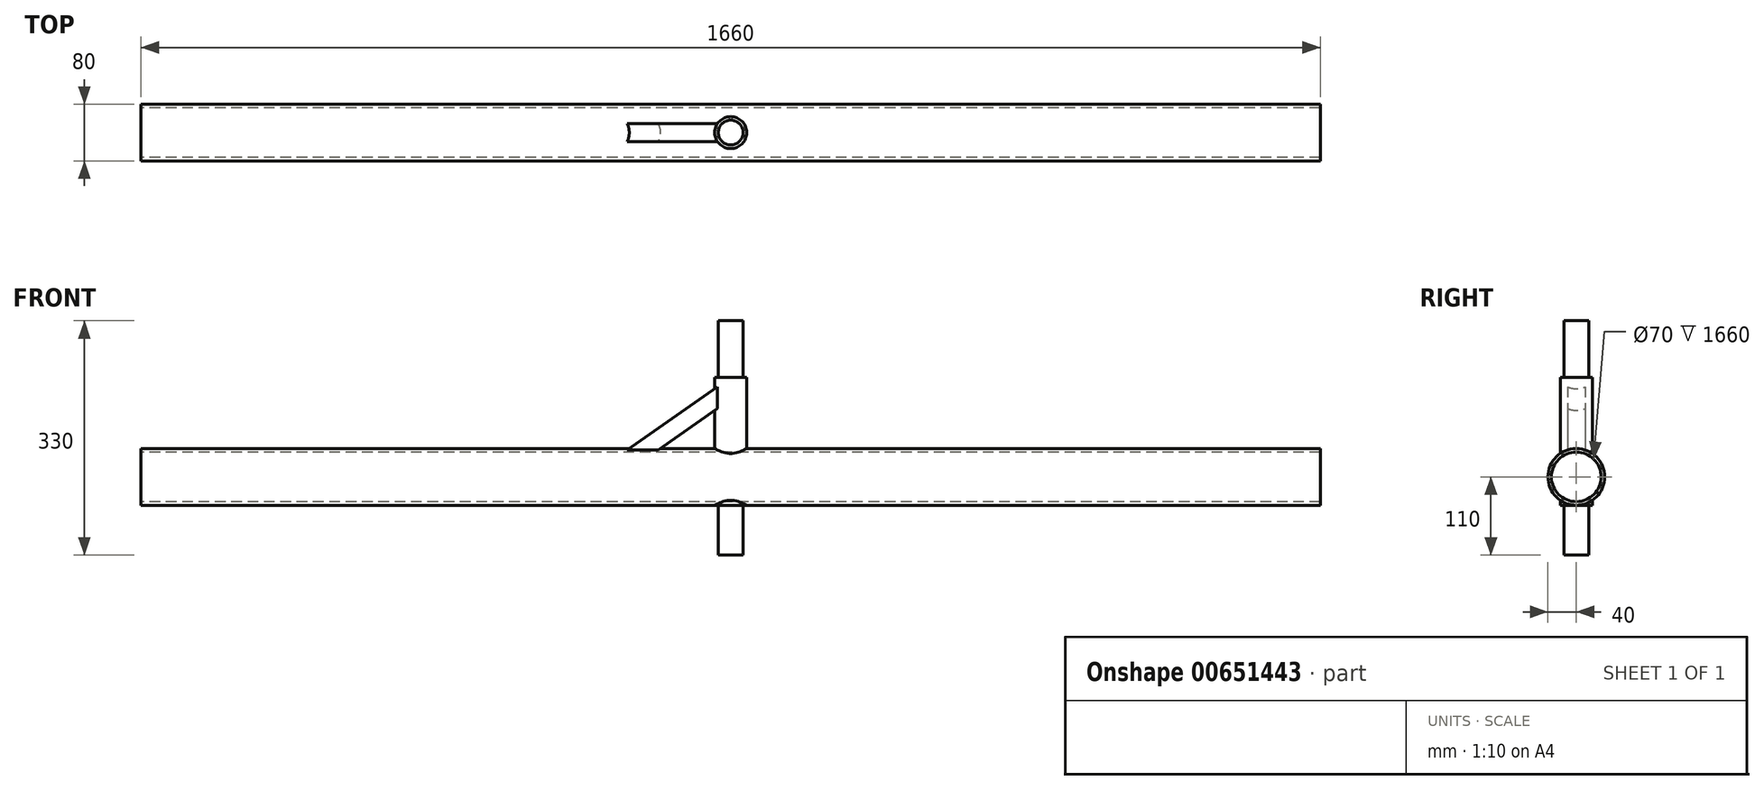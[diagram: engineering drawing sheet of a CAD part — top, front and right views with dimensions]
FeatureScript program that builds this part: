
annotation { "Feature Type Name" : "Feature", "Feature Type Description" : "" }
export const myFeature = defineFeature(function(context is Context, id is Id, definition is map)
    precondition{}
    {
        {
            var Q0;
            Q0=qCreatedBy(makeId("Right.planeOp"),FACE);
            var sketch = newSketch(context, id + "F0", { "sketchPlane" : qUnion([Q0])});
            skCircle(sketch, "E0", {"center": v(0, 0) * mm, "radius": 40 * mm});
            skSolve(sketch);
        }
        {
            var Q0;
            Q0=makeQuery(id+"F0.imprint","IMPRINT",FACE,{"disambiguationData":[TD([[makeQuery(id+"F0.imprint","IMPRINT",EDGE,{"derivedFrom":sQuery(id+"F0.wireOp",EDGE,"E0")}),1.0]])]});
            extrude(context, id + "F1", {"entities" : qUnion([Q0]), "depth" : 830 * mm, "offsetDistance" : 25 * mm, "hasSecondDirection" : true, "secondDirectionOppositeDirection" : true, "secondDirectionDepth" : 830 * mm});
        }
        {
            var Q0;
            Q0=qCreatedBy(makeId("Top.planeOp"),FACE);
            var sketch = newSketch(context, id + "F2", { "sketchPlane" : qUnion([Q0])});
            skCircle(sketch, "E1", {"center": v(0, 0) * mm, "radius": 22.5 * mm});
            skSolve(sketch);
        }
        {
            var Q0;
            Q0 = qSketchRegion(id + "F2", true);
            extrude(context, id + "F3", {"entities" : qUnion([Q0]), "operationType" : NewBodyOperationType.ADD, "depth" : 140 * mm, "offsetDistance" : 25 * mm, "hasSecondDirection" : true, "secondDirectionOppositeDirection" : true, "secondDirectionDepth" : 40 * mm});
        }
        {
            var Q0;
            Q0=makeQuery(id+"F3.opExtrude","CAP_FACE",FACE,{"disambiguationData":[OSD([sQuery(id+"F2.wireOp",EDGE,"E1")])],"isStart":false});
            var sketch = newSketch(context, id + "F4", { "sketchPlane" : qUnion([Q0])});
            skCircle(sketch, "E2", {"center": v(0, 0) * mm, "radius": 17.5 * mm});
            skSolve(sketch);
        }
        {
            var Q0;
            Q0 = qSketchRegion(id + "F4", true);
            var Q1;
            Q1=makeQuery(id+"F3.opExtrude","CAP_FACE",FACE,{"disambiguationData":[OSD([sQuery(id+"F2.wireOp",EDGE,"E1")])],"isStart":true});
            extrude(context, id + "F5", {"entities" : qUnion([Q0]), "operationType" : NewBodyOperationType.ADD, "depth" : 80 * mm, "offsetDistance" : 25 * mm, "hasSecondDirection" : true, "secondDirectionBound" : SecondDirectionBoundingType.UP_TO_SURFACE, "secondDirectionOppositeDirection" : true, "secondDirectionDepth" : 25 * mm, "secondDirectionBoundEntityFace" : qUnion([Q1]), "hasSecondDirectionOffset" : true, "secondDirectionOffsetDistance" : 70 * mm, "secondDirectionOffsetOppositeDirection" : true});
        }
        {
            var Q0;
            Q0=qCreatedBy(makeId("Front.planeOp"),FACE);
            var sketch = newSketch(context, id + "F6", { "sketchPlane" : qUnion([Q0])});
            skLineSegment(sketch, "E3", {"start": v(0, 140) * mm, "end": v(-200, 0) * mm});
            skLineSegment(sketch, "E4", {"start": v(0, 140) * mm, "end": v(0, 0) * mm});
            skLineSegment(sketch, "E5", {"start": v(0, 0) * mm, "end": v(-200, 0) * mm});
            skLineSegment(sketch, "E6.0", {"start": v(14.34, 119.52) * mm, "end": v(-185.66, -20.48) * mm});
            skSolve(sketch);
        }
        {
            var Q0;
            {var subQ0=sQuery(id+"F6.wireOp",EDGE,"E3");Q0=makeQuery(id+"F6.imprint","IMPRINT",FACE,{"disambiguationData":[TD([[makeQuery(id+"F6.imprint","IMPRINT",EDGE,{"derivedFrom":subQ0}),1.0]])]});}
            extrude(context, id + "F7", {"entities" : qUnion([Q0]), "operationType" : NewBodyOperationType.ADD, "endBound" : BoundingType.SYMMETRIC, "depth" : 25 * mm, "offsetDistance" : 25 * mm});
        }
        {
            var Q0;
            Q0=makeQuery(id+"F1.opExtrude","CAP_FACE",FACE,{"disambiguationData":[OSD([sQuery(id+"F0.wireOp",EDGE,"E0")])],"isStart":true});
            var sketch = newSketch(context, id + "F8", { "sketchPlane" : qUnion([Q0])});
            skCircle(sketch, "E7.0", {"center": v(0, 0) * mm, "radius": 35 * mm});
            skSolve(sketch);
        }
        {
            var Q0;
            Q0=makeQuery(id+"F8.imprint","IMPRINT",FACE,{"disambiguationData":[TD([[makeQuery(id+"F8.imprint","IMPRINT",EDGE,{"derivedFrom":sQuery(id+"F8.wireOp",EDGE,"E7.0")}),1.0]])]});
            extrude(context, id + "F9", {"entities" : qUnion([Q0]), "operationType" : NewBodyOperationType.REMOVE, "endBound" : BoundingType.THROUGH_ALL, "oppositeDirection" : true, "depth" : 25 * mm, "offsetDistance" : 25 * mm});
        }
    });
